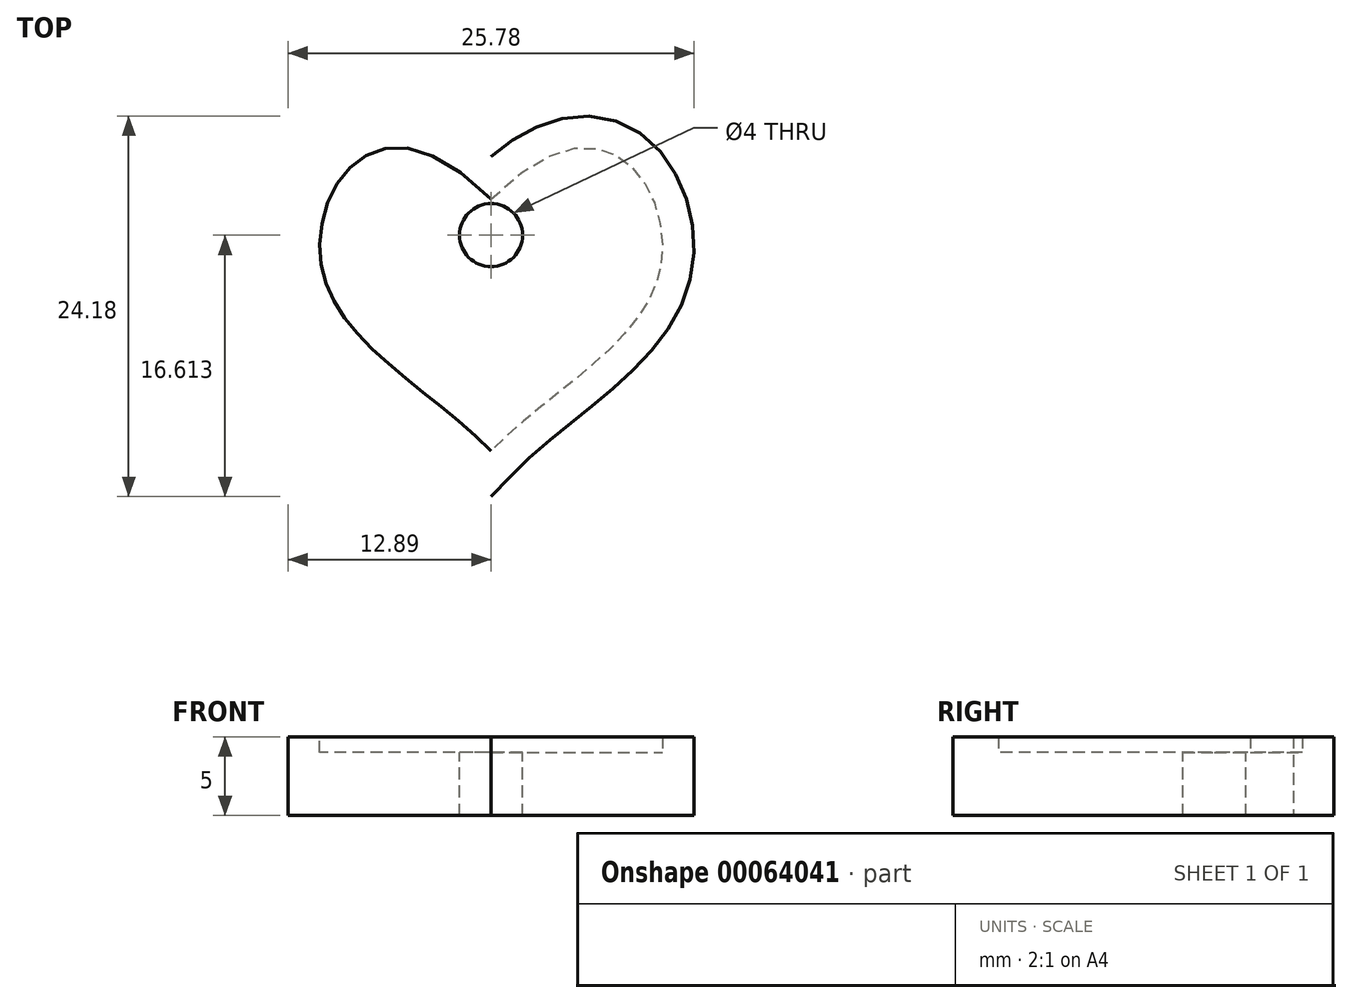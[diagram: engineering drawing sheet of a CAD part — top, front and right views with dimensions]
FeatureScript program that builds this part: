
annotation { "Feature Type Name" : "Feature", "Feature Type Description" : "" }
export const myFeature = defineFeature(function(context is Context, id is Id, definition is map)
    precondition{}
    {
        {
            var Q0;
            Q0=qCreatedBy(makeId("Top.planeOp"),FACE);
            var sketch = newSketch(context, id + "F0", { "sketchPlane" : qUnion([Q0])});
            skFitSpline(sketch, "E0", {"points": [v(0, 7.24) * mm, v(-10.88, 3.83) * mm, v(0, -8.76) * mm], "startDerivative": vector(-46.64, 47.36) * mm, "endDerivative": vector(21.83, -22.74) * mm});
            skFitSpline(sketch, "E1.MirrorCS", {"points": [v(0, 7.24) * mm, v(10.88, 3.83) * mm, v(0, -8.76) * mm], "startDerivative": vector(46.64, 47.36) * mm, "endDerivative": vector(-21.83, -22.74) * mm});
            skSolve(sketch);
        }
        {
            var Q0;
            Q0=makeQuery(id+"F0.imprint","IMPRINT",FACE,{"disambiguationData":[TD([[makeQuery(id+"F0.imprint","IMPRINT",EDGE,{"derivedFrom":sQuery(id+"F0.wireOp",EDGE,"E0")}),1.0]])]});
            extrude(context, id + "F1", {"entities" : qUnion([Q0]), "depth" : 3 * mm});
        }
        {
            var Q0;
            Q0=makeQuery(id+"F1.opExtrude","CAP_FACE",FACE,{"disambiguationData":[OSD([sQuery(id+"F0.wireOp",EDGE,"E0"),sQuery(id+"F0.wireOp",EDGE,"E1.MirrorCS")])],"isStart":false});
            shell(context, id + "F2", {"entities" : qUnion([Q0]), "thickness" : 2 * mm, "oppositeDirection" : true});
        }
        {
            var Q0;
            Q0=makeQuery(id+"F2.opShell","OFFSET_FACE",FACE,{"disambiguationData":[OSD([sQuery(id+"F0.wireOp",EDGE,"E0"),sQuery(id+"F0.wireOp",EDGE,"E1.MirrorCS")])]});
            extrude(context, id + "F3", {"entities" : qUnion([Q0]), "operationType" : NewBodyOperationType.ADD, "depth" : 2 * mm});
        }
        {
            var Q0;
            Q0=makeQuery(id+"F1.opExtrude","CAP_FACE",FACE,{"disambiguationData":[OSD([sQuery(id+"F0.wireOp",EDGE,"E0"),sQuery(id+"F0.wireOp",EDGE,"E1.MirrorCS")])],"isStart":false});
            var sketch = newSketch(context, id + "F4", { "sketchPlane" : qUnion([Q0])});
            skCircle(sketch, "E2", {"center": v(0, 4.96) * mm, "radius": 2 * mm});
            skSolve(sketch);
        }
        {
            var Q0;
            Q0=makeQuery(id+"F4.imprint","IMPRINT",FACE,{"disambiguationData":[TD([[makeQuery(id+"F4.imprint","IMPRINT",EDGE,{"derivedFrom":sQuery(id+"F4.wireOp",EDGE,"E2")}),1.0]])]});
            extrude(context, id + "F5", {"entities" : qUnion([Q0]), "operationType" : NewBodyOperationType.REMOVE, "oppositeDirection" : true, "depth" : 25 * mm});
        }
    });
